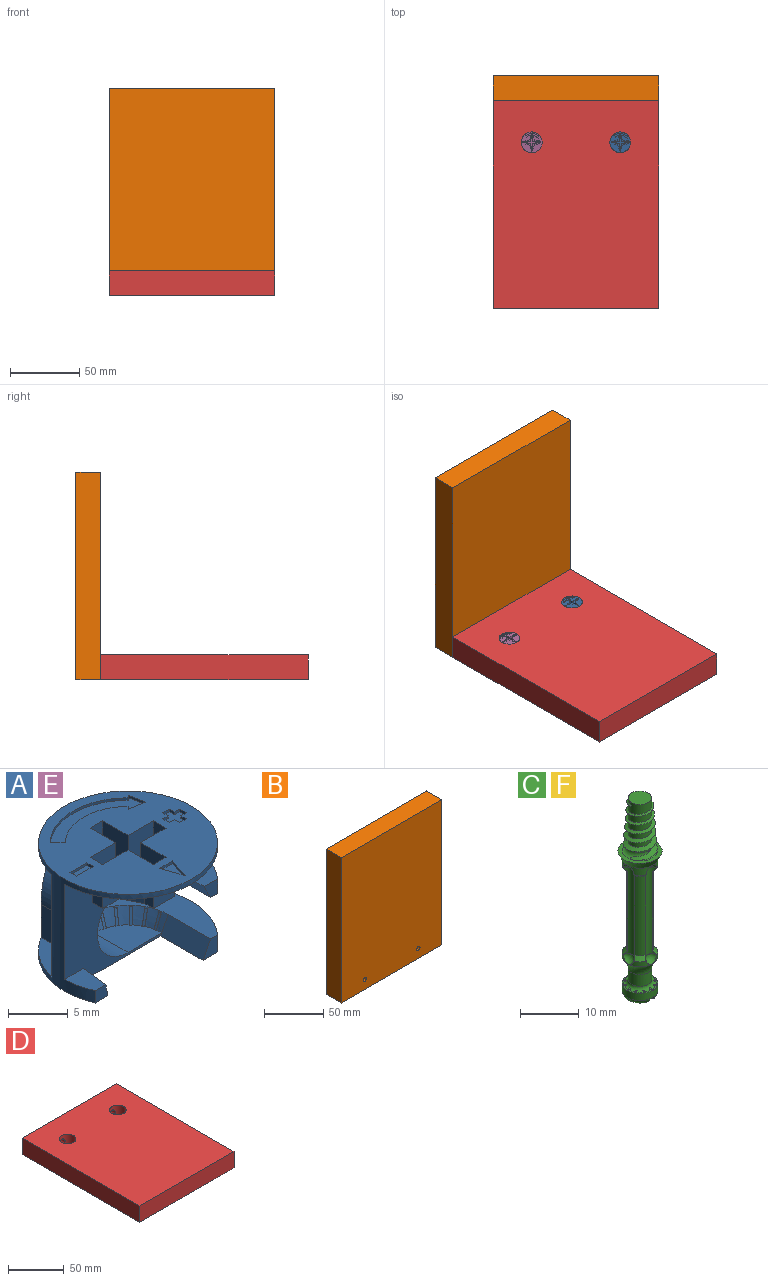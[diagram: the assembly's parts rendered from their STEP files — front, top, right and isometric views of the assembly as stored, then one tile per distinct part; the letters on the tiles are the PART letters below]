
ASSEMBLY  parts=6 mates=5
PART A: 154 faces, bbox 15x15x11.5 mm
  f0: plane 2.25x1.5mm, normal (0,1,0), area 3.4mm2, adj f1,f2,f22,f23
  f1: plane 15x15mm, normal (0,0,1), area 137.8mm2, adj f0,f2,f3,f15,f16,f17,f18,f19
  f2: plane 3x3mm, normal (-1,0,0), area 8.7mm2, adj f0,f1,f23,f24,f26
  f3: plane 2.25x1.5mm, normal (-1,0,0), area 3.4mm2, adj f1,f15,f24,f25
  f4: plane 3.25x2mm, normal (0.89,0.45,0), area 7.3mm2, adj f14,f31,f44,f49
  f5: plane 3.5x2mm, normal (-0.89,-0.45,0), area 7.8mm2, adj f9,f13,f32,f41
  f6: plane 3.5x2mm, normal (0.89,-0.45,0), area 7.8mm2, adj f7,f12,f32,f41
  f7: plane 3.5x1mm, normal (1,0,0), area 3.5mm2, adj f6,f8,f32,f41
  f8: plane 3.5x2.5mm, normal (0,-1,0), area 8.8mm2, adj f7,f13,f32,f41
  f9: plane 3.5x2mm, normal (0,-1,0), area 7mm2, adj f5,f32,f34,f41
  f10: plane 3.5x2mm, normal (0,1,0), area 7mm2, adj f33,f35,f57,f58
  f11: plane 3.46x1mm, normal (-1,0,0), area 3.5mm2, adj f29,f33,f58,f67
  f12: plane 3.5x2mm, normal (0,-1,0), area 7mm2, adj f6,f32,f36,f41,f62
  f13: plane 3.5x1mm, normal (-1,0,0), area 3.5mm2, adj f5,f8,f32,f41
  f14: plane 3.25x1mm, normal (1,0,0), area 3.3mm2, adj f4,f30,f31,f49
  f15: plane 3x3mm, normal (0,-1,0), area 8.7mm2, adj f1,f3,f25,f26,f27
  f16: plane 2.25x1.5mm, normal (0,-1,0), area 3.4mm2, adj f1,f17,f27,f28
  f17: plane 3x3mm, normal (1,0,0), area 8.7mm2, adj f1,f16,f18,f26,f28
  f18: plane 3x3mm, normal (0,-1,0), area 8.7mm2, adj f1,f17,f19,f21,f26
  f19: plane 2.25x1.5mm, normal (1,0,0), area 3.4mm2, adj f1,f18,f20,f21
  f20: plane 3x3mm, normal (0,1,0), area 8.7mm2, adj f1,f19,f21,f22,f26
  f21: plane 1.5x0.75mm, normal (0.71,0,0.71), area 1.6mm2, adj f18,f19,f20,f26
  f22: plane 3x3mm, normal (1,0,0), area 8.7mm2, adj f0,f1,f20,f23,f26
  f23: plane 1.5x0.75mm, normal (0,0.71,0.71), area 1.6mm2, adj f0,f2,f22,f26
  f24: plane 3x3mm, normal (0,1,0), area 8.7mm2, adj f1,f2,f3,f25,f26
  f25: plane 1.5x0.75mm, normal (-0.71,0,0.71), area 1.6mm2, adj f3,f15,f24,f26
  f26: plane 6x6mm, normal (0,0,1), area 15.8mm2, adj f2,f15,f17,f18,f20,f21,f22,f23
  f27: plane 3x3mm, normal (-1,0,0), area 8.7mm2, adj f1,f15,f16,f26,f28
  f28: plane 1.5x0.75mm, normal (0,-0.71,0.71), area 1.6mm2, adj f16,f17,f26,f27
  f29: plane 3.46x0.88mm, normal (0,1,0), area 2.9mm2, adj f11,f33,f53,f67
  f30: plane 3.25x0.88mm, normal (0,1,0), area 2.8mm2, adj f14,f31,f37,f49
  f31: plane 6.99x6.92mm, normal (0,0,-1), area 30.6mm2, adj f4,f14,f30,f37,f44,f45,f46,f47
  f32: plane 15x7.5mm, normal (0,0,-1), area 68.2mm2, adj f5,f6,f7,f8,f9,f12,f13,f34
  f33: plane 6.99x6.92mm, normal (0,0,-1), area 30.6mm2, adj f10,f11,f29,f35,f38,f39,f53,f56
  f34: plane 3.5x1.25mm, normal (-1,0,0), area 4.4mm2, adj f9,f32,f41,f51
  f35: plane 3.5x0.75mm, normal (-1,0,0), area 2.6mm2, adj f10,f33,f56,f57
  f36: plane 3.5x1.25mm, normal (1,0,0), area 4.4mm2, adj f12,f32,f40,f62
  f37: plane 3.25x3.24mm, normal (1,0,0), area 10.5mm2, adj f30,f31,f49,f69
  f38: plane 10.5x1.25mm, normal (0.88,0.47,0), area 14.9mm2, adj f33,f39,f55,f56
  f39: plane 10.5x0.13mm, normal (0,1,0), area 1.3mm2, adj f33,f38,f55,f69
  f40: plane 3.5x3.25mm, normal (0,-1,0), area 11.4mm2, adj f32,f36,f62,f69
  f41: plane 8.25x8.25mm, normal (0,0,-1), area 32.3mm2, adj f5,f6,f7,f8,f9,f12,f13,f34
  f42: plane 5x1.5mm, normal (-0.89,0,-0.45), area 8.4mm2, adj f41,f54,f62,f65,f149
  f43: plane 12.5x7.5mm, normal (0,0,1), area 37.2mm2, adj f50,f52,f64,f69,f70,f112
  f44: plane 3.25x2mm, normal (0,1,0), area 6.5mm2, adj f4,f31,f45,f49
  f45: plane 3.25x0.75mm, normal (1,0,0), area 2.4mm2, adj f31,f44,f46,f49
  f46: plane 3.25x2.25mm, normal (0,1,0), area 7.3mm2, adj f31,f45,f47,f49
  f47: plane 3.25x1.25mm, normal (-0.88,0.47,0), area 4.6mm2, adj f31,f46,f48,f49
  f48: plane 3.25x0.13mm, normal (0,1,0), area 0.4mm2, adj f31,f47,f49,f69
  f49: plane 6.99x6.92mm, normal (0,0,1), area 30.6mm2, adj f4,f14,f30,f37,f44,f45,f46,f47
  f50: cylinder r=2.12mm len=4.25mm, axis (0,1,0), area 18.4mm2, adj f43,f54,f69,f80
  f51: plane 11.5x11mm, normal (0,-1,0), area 45mm2, adj f32,f34,f41,f52,f60,f61,f63,f69
  f52: plane 5x1.75mm, normal (-0.89,0,0.45), area 9.8mm2, adj f43,f51,f63,f64,f112
  f53: plane 3.27x3.24mm, normal (-1,0,0), area 10.6mm2, adj f29,f33,f67,f69
  f54: plane 12.5x7.5mm, normal (0,0,-1), area 37.2mm2, adj f42,f50,f65,f68,f69,f149
  f55: plane 5.92x3.42mm, normal (0,0,1), area 13.9mm2, adj f38,f39,f56,f66,f69
  f56: plane 10.5x5.13mm, normal (0,1,0), area 28.7mm2, adj f33,f35,f38,f55,f57,f66,f67
  f57: plane 2.88x2.51mm, normal (0,0,-1), area 2.9mm2, adj f10,f35,f56,f58,f67
  f58: plane 3.5x2mm, normal (-0.89,0.45,0), area 7.8mm2, adj f10,f11,f33,f57,f67
  f59: plane 1.5x1.25mm, normal (0,-1,0), area 1.7mm2, adj f60,f61,f63,f69
  f60: plane 3x2.25mm, normal (0,0,1), area 5.6mm2, adj f51,f59,f61,f69
  f61: plane 3x1.25mm, normal (0.97,-0.12,0.2), area 3.9mm2, adj f51,f59,f60,f63
  f62: plane 5x3.5mm, normal (0,0,1), area 14.2mm2, adj f12,f36,f40,f42,f65,f68
  f63: plane 15x12.5mm, normal (0,0,-1), area 109.8mm2, adj f51,f52,f59,f61,f64,f69,f70
  f64: plane 1.75x1.72mm, normal (0,-1,0), area 2.2mm2, adj f43,f52,f63,f70
  f65: plane 1.59x1.5mm, normal (0,-1,0), area 1.8mm2, adj f42,f54,f62,f68
  f66: plane 5.92x3.38mm, normal (-1,0,0), area 20mm2, adj f55,f56,f67,f69
  f67: cylinder r=3.88mm len=6.99mm, axis (0,-1,0), area 33.2mm2, adj f11,f29,f53,f56,f57,f58,f66,f69
  f68: cylinder r=7.5mm len=5mm, axis (0,0,-1), area 8.2mm2, adj f54,f62,f65,f69
  f69: cylinder r=7.5mm len=15mm, axis (0,0,-1), area 120.2mm2, adj f1,f31,f32,f33,f37,f39,f40,f43
  f70: cylinder r=7.5mm len=5mm, axis (0,0,-1), area 9.6mm2, adj f43,f63,f64,f69
  f71: plane 2.25x1.5mm, normal (0,0,1), area 1.7mm2, adj f72,f73,f74
  f72: plane 2.25x0.75mm, normal (0.95,0.32,0), area 0.6mm2, adj f1,f71,f73,f74
  f73: plane 1.5x0.25mm, normal (0,-1,0), area 0.4mm2, adj f1,f71,f72,f74
  f74: plane 2.25x0.75mm, normal (-0.95,0.32,0), area 0.6mm2, adj f1,f71,f72,f73
  f75: cylinder r=3.62mm len=7.25mm, axis (0,1,0), area 45.5mm2, adj f41,f51,f76,f77,f80,f82,f83,f111
  f76: plane 1.41x0.71mm, normal (0,-0.89,0.45), area 0.4mm2, adj f75,f77,f78,f79,f111
  f77: plane 1.42x0.76mm, normal (-1,0,0), area 0.1mm2, adj f75,f76,f78,f80
  f78: plane 0.25x0.05mm, normal (0,0.45,0.89), area 0mm2, adj f76,f77,f79,f80,f112
  f79: plane 1.41x0.75mm, normal (1,0,0), area 0.1mm2, adj f76,f78,f111,f112
  f80: cone r=2.88mm half-angle=63.4deg, axis (0,-1,0), area 14.7mm2, adj f50,f75,f77,f78,f81,f82,f112,f149
  f81: plane 0.25x0.05mm, normal (0,0.45,-0.89), area 0mm2, adj f80,f82,f83,f84,f149
  f82: plane 1.42x0.76mm, normal (-1,0,0), area 0.1mm2, adj f75,f80,f81,f83
  f83: plane 1.41x0.71mm, normal (0,-0.89,-0.45), area 0.4mm2, adj f41,f75,f81,f82,f84
  f84: plane 1.41x0.75mm, normal (1,0,0), area 0.1mm2, adj f41,f81,f83,f149
  f85: plane 0.75x0.25mm, normal (0,-1,0), area 0.2mm2, adj f1,f89,f90,f91
  f86: plane 0.63x0.25mm, normal (-1,0,0), area 0.2mm2, adj f1,f87,f91,f97
  f87: plane 0.75x0.25mm, normal (0,1,0), area 0.2mm2, adj f1,f86,f88,f91
  f88: plane 0.63x0.25mm, normal (1,0,0), area 0.2mm2, adj f1,f87,f91,f96
  f89: plane 0.63x0.25mm, normal (-1,0,0), area 0.2mm2, adj f1,f85,f91,f95
  f90: plane 0.63x0.25mm, normal (1,0,0), area 0.2mm2, adj f1,f85,f91,f92
  f91: plane 2x2mm, normal (0,0,1), area 2.4mm2, adj f85,f86,f87,f88,f89,f90,f92,f93
  f92: plane 0.63x0.25mm, normal (0,-1,0), area 0.2mm2, adj f1,f90,f91,f94
  f93: plane 0.75x0.25mm, normal (-1,0,0), area 0.2mm2, adj f1,f91,f95,f97
  f94: plane 0.75x0.25mm, normal (1,0,0), area 0.2mm2, adj f1,f91,f92,f96
  f95: plane 0.63x0.25mm, normal (0,-1,0), area 0.2mm2, adj f1,f89,f91,f93
  f96: plane 0.63x0.25mm, normal (0,1,0), area 0.2mm2, adj f1,f88,f91,f94
  f97: plane 0.63x0.25mm, normal (0,1,0), area 0.2mm2, adj f1,f86,f91,f93
  f98: plane 2x0.75mm, normal (0,0,1), area 1.5mm2, adj f99,f100,f101,f102
  f99: plane 2x0.25mm, normal (0,-1,0), area 0.5mm2, adj f1,f98,f100,f102
  f100: plane 0.75x0.25mm, normal (-1,0,0), area 0.2mm2, adj f1,f98,f99,f101
  f101: plane 2x0.25mm, normal (0,1,0), area 0.5mm2, adj f1,f98,f100,f102
  f102: plane 0.75x0.25mm, normal (1,0,0), area 0.2mm2, adj f1,f98,f99,f101
  f103: plane 9.81x3.41mm, normal (0,0,1), area 13mm2, adj f104,f105,f106,f107,f108,f109,f110
  f104: plane 1.77x0.35mm, normal (-0.98,-0.2,0), area 0.5mm2, adj f1,f103,f105,f110
  f105: plane 1.77x0.35mm, normal (0.2,0.98,0), area 0.5mm2, adj f1,f103,f104,f106
  f106: plane 0.27x0.27mm, normal (0.71,-0.71,0), area 0.1mm2, adj f1,f103,f105,f107
  f107: cylinder r=5.25mm len=7.42mm, axis (0,0,-1), area 2.1mm2, adj f1,f103,f106,f108
  f108: plane 0.88x0.88mm, normal (0.71,0.71,0), area 0.3mm2, adj f1,f103,f107,f109
  f109: cylinder r=6.5mm len=9.19mm, axis (0,0,1), area 2.6mm2, adj f1,f103,f108,f110
  f110: plane 0.27x0.27mm, normal (0.71,-0.71,0), area 0.1mm2, adj f1,f103,f104,f109
  f111: plane 4x4mm, normal (0,0,1), area 12.5mm2, adj f51,f75,f76,f79,f112,f113,f114,f115
  f112: cone r=4.38mm half-angle=26.6deg, axis (0,0,1), area 9.4mm2, adj f43,f52,f78,f79,f80,f111,f114,f115
  f113: plane 1.41x0.75mm, normal (-0.25,-0.86,0.45), area 0.4mm2, adj f111,f114,f115,f116
  f114: plane 1.41x0.72mm, normal (0.96,-0.28,0), area 0.1mm2, adj f111,f112,f113,f116
  f115: plane 1.41x0.72mm, normal (-0.96,0.28,0), area 0.1mm2, adj f111,f112,f113,f116
  f116: plane 0.25x0.11mm, normal (0.12,0.43,0.89), area 0mm2, adj f112,f113,f114,f115
  f117: plane 1.41x0.73mm, normal (-0.47,-0.76,0.45), area 0.4mm2, adj f111,f118,f119,f120
  f118: plane 1.41x0.64mm, normal (0.85,-0.53,0), area 0.1mm2, adj f111,f112,f117,f120
  f119: plane 1.41x0.64mm, normal (-0.85,0.53,0), area 0.1mm2, adj f111,f112,f117,f120
  f120: plane 0.24x0.17mm, normal (0.24,0.38,0.89), area 0mm2, adj f112,f117,f118,f119
  f121: plane 1.41x0.69mm, normal (-0.66,-0.6,0.45), area 0.4mm2, adj f111,f122,f123,f124
  f122: plane 1.41x0.56mm, normal (0.67,-0.74,0), area 0.1mm2, adj f111,f112,f121,f124
  f123: plane 1.41x0.56mm, normal (-0.67,0.74,0), area 0.1mm2, adj f111,f112,f121,f124
  f124: plane 0.22x0.2mm, normal (0.33,0.3,0.89), area 0mm2, adj f112,f121,f122,f123
  f125: plane 1.41x0.74mm, normal (-0.8,-0.39,0.45), area 0.4mm2, adj f111,f126,f127,f128
  f126: plane 1.41x0.67mm, normal (0.44,-0.9,0), area 0.1mm2, adj f111,f112,f125,f128
  f127: plane 1.41x0.67mm, normal (-0.44,0.9,0), area 0.1mm2, adj f111,f112,f125,f128
  f128: plane 0.25x0.15mm, normal (0.4,0.2,0.89), area 0mm2, adj f112,f125,f126,f127
  f129: plane 1.41x0.74mm, normal (-0.88,-0.16,0.45), area 0.4mm2, adj f111,f130,f131,f132
  f130: plane 1.41x0.74mm, normal (0.17,-0.98,0), area 0.1mm2, adj f111,f112,f129,f132
  f131: plane 1.41x0.74mm, normal (-0.17,0.98,0), area 0.1mm2, adj f111,f112,f129,f132
  f132: plane 0.26x0.09mm, normal (0.44,0.08,0.89), area 0mm2, adj f112,f129,f130,f131
  f133: plane 0.25x0.11mm, normal (0.12,0.43,-0.89), area 0mm2, adj f134,f135,f136,f149
  f134: plane 1.41x0.72mm, normal (0.96,-0.28,0), area 0.1mm2, adj f41,f133,f136,f149
  f135: plane 1.41x0.72mm, normal (-0.96,0.28,0), area 0.1mm2, adj f41,f133,f136,f149
  f136: plane 1.41x0.75mm, normal (-0.25,-0.86,-0.45), area 0.4mm2, adj f41,f133,f134,f135
  f137: plane 0.24x0.17mm, normal (0.24,0.38,-0.89), area 0mm2, adj f138,f139,f140,f149
  f138: plane 1.41x0.64mm, normal (0.85,-0.53,0), area 0.1mm2, adj f41,f137,f140,f149
  f139: plane 1.41x0.64mm, normal (-0.85,0.53,0), area 0.1mm2, adj f41,f137,f140,f149
  f140: plane 1.41x0.73mm, normal (-0.47,-0.76,-0.45), area 0.4mm2, adj f41,f137,f138,f139
  f141: plane 0.22x0.2mm, normal (0.33,0.3,-0.89), area 0mm2, adj f142,f143,f144,f149
  f142: plane 1.41x0.56mm, normal (0.67,-0.74,0), area 0.1mm2, adj f41,f141,f144,f149
  f143: plane 1.41x0.56mm, normal (-0.67,0.74,0), area 0.1mm2, adj f41,f141,f144,f149
  f144: plane 1.41x0.69mm, normal (-0.66,-0.6,-0.45), area 0.4mm2, adj f41,f141,f142,f143
  f145: plane 0.25x0.15mm, normal (0.4,0.2,-0.89), area 0mm2, adj f146,f147,f148,f149
  f146: plane 1.41x0.67mm, normal (0.44,-0.9,0), area 0.1mm2, adj f41,f145,f148,f149
  f147: plane 1.41x0.67mm, normal (-0.44,0.9,0), area 0.1mm2, adj f41,f145,f148,f149
  f148: plane 1.41x0.74mm, normal (-0.8,-0.39,-0.45), area 0.4mm2, adj f41,f145,f146,f147
  f149: cone r=4.75mm half-angle=26.6deg, axis (0,0,-1), area 9.4mm2, adj f41,f42,f54,f80,f81,f84,f133,f134
  f150: plane 0.26x0.09mm, normal (0.44,0.08,-0.89), area 0mm2, adj f149,f151,f152,f153
  f151: plane 1.41x0.74mm, normal (0.17,-0.98,0), area 0.1mm2, adj f41,f149,f150,f153
  f152: plane 1.41x0.74mm, normal (-0.17,0.98,0), area 0.1mm2, adj f41,f149,f150,f153
  f153: plane 1.41x0.74mm, normal (-0.88,-0.16,-0.45), area 0.4mm2, adj f41,f150,f151,f152
PART B: 10 faces, bbox 120x18x150 mm
  f0: plane 150x18mm, normal (-1,0,0), area 2700mm2, adj f1,f3,f4,f5
  f1: plane 120x18mm, normal (0,0,-1), area 2160mm2, adj f0,f2,f4,f5
  f2: plane 150x18mm, normal (1,0,0), area 2700mm2, adj f1,f3,f4,f5
  f3: plane 120x18mm, normal (0,0,1), area 2160mm2, adj f0,f2,f4,f5
  f4: plane 150x120mm, normal (0,-1,0), area 17974.9mm2, adj f0,f1,f2,f3,f6,f8
  f5: plane 150x120mm, normal (0,1,0), area 18000mm2, adj f0,f1,f2,f3
  f6: cylinder r=2mm len=11mm, axis (0,-1,0), area 138.2mm2, adj f4,f7
  f7: plane 4x4mm, normal (0,-1,0), area 12.6mm2, adj f6
  f8: cylinder r=2mm len=11mm, axis (0,-1,0), area 138.2mm2, adj f4,f9
  f9: plane 4x4mm, normal (0,-1,0), area 12.6mm2, adj f8
PART C: 132 faces, bbox 8.2x8.2x41.2 mm
  f0: plane 2.21x2.07mm, normal (0,-1,-0.09), area 3.9mm2, adj f1,f6,f8,f9,f17
  f1: plane 2.52x2.17mm, normal (1,0,-0.09), area 3.8mm2, adj f0,f6,f8,f16,f17,f20
  f2: plane 2.52x2.17mm, normal (-1,0,-0.09), area 3.8mm2, adj f3,f6,f13,f16,f19,f20
  f3: plane 2.21x2.07mm, normal (0,-1,-0.09), area 3.9mm2, adj f2,f6,f12,f13,f19
  f4: plane 2.52x2.17mm, normal (1,0,-0.09), area 3.8mm2, adj f5,f6,f10,f11,f17,f18
  f5: plane 2.21x2.07mm, normal (0,1,-0.09), area 3.9mm2, adj f4,f6,f9,f10,f17
  f6: plane 5.15x4.83mm, normal (0,0,-1), area 10.1mm2, adj f0,f1,f2,f3,f4,f5,f7,f9
  f7: plane 2.21x2.07mm, normal (0,1,-0.09), area 3.9mm2, adj f6,f12,f14,f15,f19
  f8: plane 1.1x1.1mm, normal (0,0,-1), area 0.8mm2, adj f0,f1,f17
  f9: plane 1.69x1.43mm, normal (1,0,-0.09), area 2.2mm2, adj f0,f5,f6,f17
  f10: plane 1.1x1.1mm, normal (0,0,-1), area 0.8mm2, adj f4,f5,f17
  f11: plane 1.33x1mm, normal (0,1,-0.09), area 1.2mm2, adj f4,f6,f14,f18
  f12: plane 1.69x1.43mm, normal (-1,0,-0.09), area 2.2mm2, adj f3,f6,f7,f19
  f13: plane 1.1x1.1mm, normal (0,0,-1), area 0.8mm2, adj f2,f3,f19
  f14: plane 2.52x2.17mm, normal (-1,0,-0.09), area 3.8mm2, adj f6,f7,f11,f15,f18,f19
  f15: plane 1.1x1.1mm, normal (0,0,-1), area 0.8mm2, adj f7,f14,f19
  f16: plane 1.33x1mm, normal (0,-1,-0.09), area 1.2mm2, adj f1,f2,f6,f20
  f17: torus R=2mm, axis (0,0,1), area 9.2mm2, adj f0,f1,f4,f5,f8,f9,f10,f32
  f18: plane 1.33x0.5mm, normal (0,0,-1), area 0.6mm2, adj f4,f11,f14,f32
  f19: torus R=2mm, axis (0,0,1), area 9.2mm2, adj f2,f3,f7,f12,f13,f14,f15,f32
  f20: plane 1.33x0.5mm, normal (0,0,-1), area 0.6mm2, adj f1,f2,f16,f32
  f21: torus R=2.88mm, axis (0,0,1), area 0mm2, adj f32,f36,f37,f38
  f22: torus R=2.88mm, axis (0,0,1), area 0mm2, adj f32,f40,f41,f42
  f23: torus R=2.88mm, axis (0,0,1), area 0mm2, adj f32,f44,f45,f46
  f24: torus R=2.88mm, axis (0,0,1), area 0mm2, adj f32,f48,f49,f50
  f25: torus R=2.88mm, axis (0,0,1), area 0mm2, adj f32,f52,f53,f54
  f26: torus R=2.88mm, axis (0,0,1), area 0mm2, adj f32,f56,f57,f58
  f27: torus R=2.88mm, axis (0,0,1), area 0mm2, adj f32,f60,f61,f62
  f28: torus R=2.88mm, axis (0,0,1), area 0mm2, adj f32,f64,f65,f66
  f29: torus R=2.88mm, axis (0,0,1), area 0mm2, adj f32,f68,f69,f70
  f30: torus R=2.88mm, axis (0,0,1), area 0mm2, adj f32,f72,f73,f74
  f31: torus R=2.88mm, axis (0,0,1), area 0mm2, adj f32,f76,f77,f78
  f32: cylinder r=3mm len=6mm, axis (0,0,-1), area 28.3mm2, adj f17,f18,f19,f20,f21,f22,f23,f24
  f33: torus R=2.88mm, axis (0,0,1), area 0mm2, adj f32,f34,f80,f81
  f34: plane 0.58x0.34mm, normal (-0.87,0.5,0), area 0.1mm2, adj f33,f35,f81,f82
  f35: plane 1.27x0.56mm, normal (0,0,1), area 0.3mm2, adj f32,f34,f36,f82
  f36: plane 0.67x0.13mm, normal (1,0,0), area 0.1mm2, adj f21,f35,f37,f82
  f37: plane 0.54x0.25mm, normal (0,0,1), area 0.1mm2, adj f21,f36,f38,f82
  f38: plane 0.67x0.13mm, normal (-1,0,0), area 0.1mm2, adj f21,f37,f39,f82
  f39: plane 1.27x0.56mm, normal (0,0,1), area 0.3mm2, adj f32,f38,f40,f82
  f40: plane 0.58x0.34mm, normal (0.87,0.5,0), area 0.1mm2, adj f22,f39,f41,f82
  f41: plane 0.59x0.49mm, normal (0,0,1), area 0.1mm2, adj f22,f40,f42,f82
  f42: plane 0.58x0.34mm, normal (-0.87,-0.5,0), area 0.1mm2, adj f22,f41,f43,f82
  f43: plane 1.05x1.05mm, normal (0,0,1), area 0.3mm2, adj f32,f42,f44,f82
  f44: plane 0.58x0.34mm, normal (0.5,0.87,0), area 0.1mm2, adj f23,f43,f45,f82
  f45: plane 0.59x0.49mm, normal (0,0,1), area 0.1mm2, adj f23,f44,f46,f82
  f46: plane 0.58x0.34mm, normal (-0.5,-0.87,0), area 0.1mm2, adj f23,f45,f47,f82
  f47: plane 1.27x0.56mm, normal (0,0,1), area 0.3mm2, adj f32,f46,f48,f82
  f48: plane 0.67x0.13mm, normal (0,1,0), area 0.1mm2, adj f24,f47,f49,f82
  f49: plane 0.54x0.25mm, normal (0,0,1), area 0.1mm2, adj f24,f48,f50,f82
  f50: plane 0.67x0.13mm, normal (0,-1,0), area 0.1mm2, adj f24,f49,f51,f82
  f51: plane 1.27x0.56mm, normal (0,0,1), area 0.3mm2, adj f32,f50,f52,f82
  f52: plane 0.58x0.34mm, normal (-0.5,0.87,0), area 0.1mm2, adj f25,f51,f53,f82
  f53: plane 0.59x0.49mm, normal (0,0,1), area 0.1mm2, adj f25,f52,f54,f82
  f54: plane 0.58x0.34mm, normal (0.5,-0.87,0), area 0.1mm2, adj f25,f53,f55,f82
  f55: plane 1.05x1.05mm, normal (0,0,1), area 0.3mm2, adj f32,f54,f56,f82
  f56: plane 0.58x0.34mm, normal (-0.87,0.5,0), area 0.1mm2, adj f26,f55,f57,f82
  f57: plane 0.59x0.49mm, normal (0,0,1), area 0.1mm2, adj f26,f56,f58,f82
  f58: plane 0.58x0.34mm, normal (0.87,-0.5,0), area 0.1mm2, adj f26,f57,f59,f82
  f59: plane 1.27x0.56mm, normal (0,0,1), area 0.3mm2, adj f32,f58,f60,f82
  f60: plane 0.67x0.13mm, normal (-1,0,0), area 0.1mm2, adj f27,f59,f61,f82
  f61: plane 0.54x0.25mm, normal (0,0,1), area 0.1mm2, adj f27,f60,f62,f82
  f62: plane 0.67x0.13mm, normal (1,0,0), area 0.1mm2, adj f27,f61,f63,f82
  f63: plane 1.27x0.56mm, normal (0,0,1), area 0.3mm2, adj f32,f62,f64,f82
  f64: plane 0.58x0.34mm, normal (-0.87,-0.5,0), area 0.1mm2, adj f28,f63,f65,f82
  f65: plane 0.59x0.49mm, normal (0,0,1), area 0.1mm2, adj f28,f64,f66,f82
  f66: plane 0.58x0.34mm, normal (0.87,0.5,0), area 0.1mm2, adj f28,f65,f67,f82
  f67: plane 1.05x1.05mm, normal (0,0,1), area 0.3mm2, adj f32,f66,f68,f82
  f68: plane 0.58x0.34mm, normal (-0.5,-0.87,0), area 0.1mm2, adj f29,f67,f69,f82
  f69: plane 0.59x0.49mm, normal (0,0,1), area 0.1mm2, adj f29,f68,f70,f82
  f70: plane 0.58x0.34mm, normal (0.5,0.87,0), area 0.1mm2, adj f29,f69,f71,f82
  f71: plane 1.27x0.56mm, normal (0,0,1), area 0.3mm2, adj f32,f70,f72,f82
  f72: plane 0.67x0.13mm, normal (0,-1,0), area 0.1mm2, adj f30,f71,f73,f82
  f73: plane 0.54x0.25mm, normal (0,0,1), area 0.1mm2, adj f30,f72,f74,f82
  f74: plane 0.67x0.13mm, normal (0,1,0), area 0.1mm2, adj f30,f73,f75,f82
  f75: plane 1.27x0.56mm, normal (0,0,1), area 0.3mm2, adj f32,f74,f76,f82
  f76: plane 0.58x0.34mm, normal (0.5,-0.87,0), area 0.1mm2, adj f31,f75,f77,f82
  f77: plane 0.59x0.49mm, normal (0,0,1), area 0.1mm2, adj f31,f76,f78,f82
  f78: plane 0.58x0.34mm, normal (-0.5,0.87,0), area 0.1mm2, adj f31,f77,f79,f82
  f79: plane 1.05x1.05mm, normal (0,0,1), area 0.3mm2, adj f32,f78,f80,f82
  f80: plane 0.58x0.34mm, normal (0.87,-0.5,0), area 0.1mm2, adj f33,f79,f81,f82
  f81: plane 0.59x0.49mm, normal (0,0,1), area 0.1mm2, adj f33,f34,f80,f82
  f82: torus R=2.75mm, axis (0,0,1), area 15.5mm2, adj f34,f35,f36,f37,f38,f39,f40,f41
  f83: cylinder r=2mm len=4mm, axis (0,0,-1), area 30.2mm2, adj f82,f84
  f84: torus R=5.25mm, axis (0,0,1), area 37.3mm2, adj f83,f85
  f85: cone r=3mm half-angle=45deg, axis (0,0,1), area 1.3mm2, adj f84,f86,f87,f88,f89
  f86: cylinder r=3mm len=3mm, axis (0,0,-1), area 3.5mm2, adj f85,f91,f92,f93
  f87: cylinder r=3mm len=3mm, axis (0,0,-1), area 3.5mm2, adj f85,f90,f91,f95
  f88: cylinder r=3mm len=3mm, axis (0,0,-1), area 3.5mm2, adj f85,f93,f94,f96
  f89: cylinder r=3mm len=3mm, axis (0,0,-1), area 3.5mm2, adj f85,f95,f96,f97
  f90: cone r=2.25mm half-angle=45deg, axis (0,0,-1), area 2mm2, adj f87,f91,f95,f98,f99,f103
  f91: sphere r=1.25mm, area 4.3mm2, adj f86,f87,f90,f92,f99
  f92: cone r=2.25mm half-angle=45deg, axis (0,0,-1), area 2mm2, adj f86,f91,f93,f99,f100,f101
  f93: sphere r=1.25mm, area 4.3mm2, adj f86,f88,f92,f94,f101
  f94: cone r=2.25mm half-angle=45deg, axis (0,0,-1), area 2mm2, adj f88,f93,f96,f101,f102,f104
  f95: sphere r=1.25mm, area 4.4mm2, adj f87,f89,f90,f97,f103
  f96: sphere r=1.25mm, area 4.3mm2, adj f88,f89,f94,f97,f104
  f97: cone r=2.25mm half-angle=45deg, axis (0,0,-1), area 2mm2, adj f89,f95,f96,f103,f104,f105
  f98: cylinder r=2.25mm len=16.5mm, axis (0,0,-1), area 29.6mm2, adj f90,f99,f103,f106
  f99: cylinder r=1.25mm len=18mm, axis (0,0,-1), area 34.9mm2, adj f90,f91,f92,f98,f100,f106,f107,f108
  f100: cylinder r=2.25mm len=16.5mm, axis (0,0,-1), area 29.6mm2, adj f92,f99,f101,f108
  f101: cylinder r=1.25mm len=18mm, axis (0,0,-1), area 34.9mm2, adj f92,f93,f94,f100,f102,f108,f109,f110
  f102: cylinder r=2.25mm len=16.5mm, axis (0,0,-1), area 29.6mm2, adj f94,f101,f104,f110
  f103: cylinder r=1.25mm len=18mm, axis (0,0,-1), area 34.9mm2, adj f90,f95,f97,f98,f105,f106,f111,f113
  f104: cylinder r=1.25mm len=18mm, axis (0,0,-1), area 34.9mm2, adj f94,f96,f97,f102,f105,f110,f112,f113
  f105: cylinder r=2.25mm len=16.5mm, axis (0,0,-1), area 29.6mm2, adj f97,f103,f104,f113
  f106: cone r=3mm half-angle=45deg, axis (0,0,1), area 2mm2, adj f98,f99,f103,f114
  f107: sphere r=1.25mm, area 4.4mm2, adj f99,f114,f115
  f108: cone r=3mm half-angle=45deg, axis (0,0,1), area 2mm2, adj f99,f100,f101,f115
  f109: sphere r=1.25mm, area 4.4mm2, adj f101,f115,f116
  f110: cone r=3mm half-angle=45deg, axis (0,0,1), area 2mm2, adj f101,f102,f104,f116
  f111: sphere r=1.25mm, area 4.4mm2, adj f103,f114,f117
  f112: sphere r=1.25mm, area 4.4mm2, adj f104,f116,f117
  f113: cone r=3mm half-angle=45deg, axis (0,0,1), area 2mm2, adj f103,f104,f105,f117
  f114: cylinder r=3mm len=3mm, axis (0,0,-1), area 4mm2, adj f99,f103,f106,f107,f111,f118
  f115: cylinder r=3mm len=3mm, axis (0,0,-1), area 4mm2, adj f99,f101,f107,f108,f109,f118
  f116: cylinder r=3mm len=3mm, axis (0,0,-1), area 4mm2, adj f101,f104,f109,f110,f112,f118
  f117: cylinder r=3mm len=3mm, axis (0,0,-1), area 4mm2, adj f103,f104,f111,f112,f113,f118
  f118: cone r=3.75mm half-angle=26.6deg, axis (0,0,1), area 35.6mm2, adj f114,f115,f116,f117,f120
  f119: plane 4x4mm, normal (0,0,1), area 12.6mm2, adj f131
  f120: plane 7.5x7.5mm, normal (0,0,1), area 15.9mm2, adj f118,f123
  f121: plane 0.27x0.2mm, normal (0,-1,0), area 0mm2, adj f122,f125,f131
  f122: bspline ~10.74x5.67mm, area 55.8mm2, adj f121,f123,f125,f126,f127,f128,f129,f130
  f123: torus R=3mm, axis (0,0,1), area 17.2mm2, adj f120,f122,f124,f125,f126
  f124: torus R=3mm, axis (0,0,1), area 0.4mm2, adj f123,f125,f126
  f125: bspline ~10.83x6.79mm, area 59.1mm2, adj f121,f122,f123,f124,f126,f127,f128,f129
  f126: cylinder r=2mm len=4mm, axis (0,0,-1), area 8.6mm2, adj f122,f123,f124,f125,f127
  f127: cylinder r=2mm len=4mm, axis (0,0,-1), area 14.6mm2, adj f122,f125,f126,f128
  f128: cylinder r=2mm len=4mm, axis (0,0,-1), area 15.7mm2, adj f122,f125,f127,f129
  f129: cylinder r=2mm len=4mm, axis (0,0,-1), area 16.9mm2, adj f122,f125,f128,f130
  f130: cylinder r=2mm len=4mm, axis (0,0,-1), area 18mm2, adj f122,f125,f129,f131
  f131: cylinder r=2mm len=4mm, axis (0,0,-1), area 21.7mm2, adj f119,f121,f122,f125,f130
PART D: 12 faces, bbox 120x150x18 mm
  f0: plane 120x18mm, normal (0,1,0), area 2083mm2, adj f1,f3,f4,f5,f10,f11
  f1: plane 150x18mm, normal (-1,0,0), area 2700mm2, adj f0,f2,f4,f5
  f2: plane 120x18mm, normal (0,-1,0), area 2160mm2, adj f1,f3,f4,f5
  f3: plane 150x18mm, normal (1,0,0), area 2700mm2, adj f0,f2,f4,f5
  f4: plane 150x120mm, normal (0,0,1), area 17646.6mm2, adj f0,f1,f2,f3,f6,f8
  f5: plane 150x120mm, normal (0,0,-1), area 18000mm2, adj f0,f1,f2,f3
  f6: cylinder r=7.5mm len=15mm, axis (0,0,1), area 525.9mm2, adj f4,f7,f11
  f7: plane 15x15mm, normal (0,0,1), area 176.7mm2, adj f6
  f8: cylinder r=7.5mm len=15mm, axis (0,0,1), area 525.9mm2, adj f4,f9,f10
  f9: plane 15x15mm, normal (0,0,1), area 176.7mm2, adj f8
  f10: cylinder r=3.5mm len=23.37mm, axis (0,1,0), area 504.2mm2, adj f0,f8
  f11: cylinder r=3.5mm len=23.37mm, axis (0,1,0), area 504.2mm2, adj f0,f6
PART E: same geometry as A
PART F: same geometry as C
PLACE A rot(axis=(0,0.09,1),0deg) t=(92,-30,18)mm
PLACE B t=(0,18,0)mm fixed
PLACE C rot(axis=(-1,0,0),90deg) t=(28,-30,10.37)mm
PLACE D at identity
PLACE E t=(28,-30,18)mm
PLACE F rot(axis=(-1,0,0),90deg) t=(92,-30,10.38)mm
MATE fastened F.f118 <-> B.f6  axis (0,1,0) through (92,0,10.38)mm
MATE slider D.f0 <-> B.f4  axis (0,1,0) through (60,0,0)mm
MATE revolute A.f68 <-> D.f6  axis (0,0,1) through (92,-30,18)mm
MATE fastened C.f123 <-> B.f8  axis (0,1,0) through (28,0,10.37)mm
MATE revolute E.f68 <-> D.f8  axis (0,0,1) through (28,-30,18)mm
